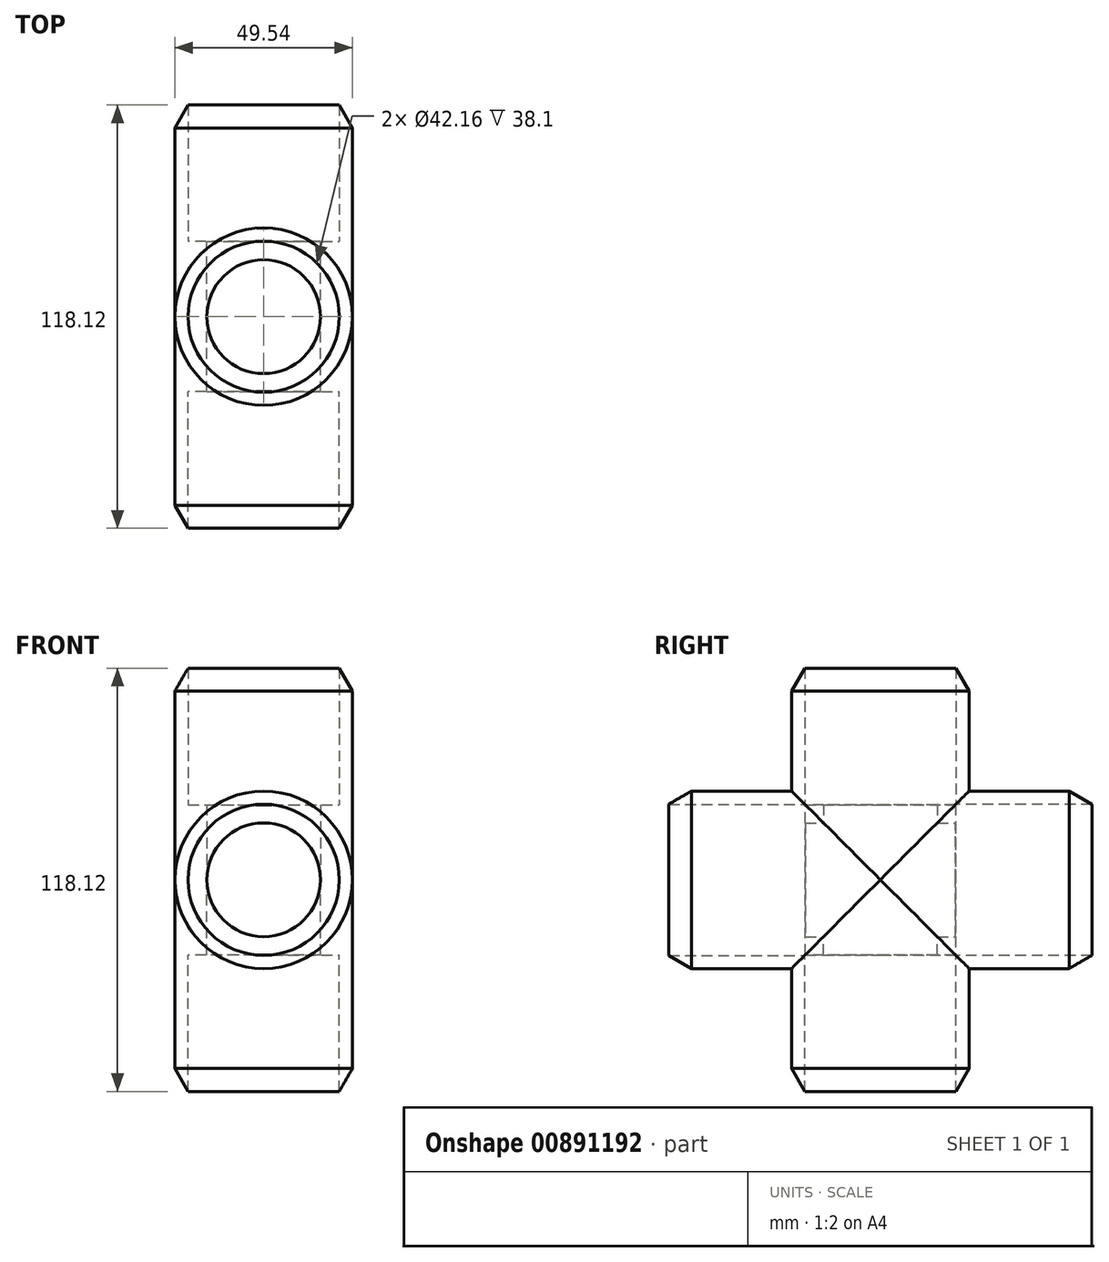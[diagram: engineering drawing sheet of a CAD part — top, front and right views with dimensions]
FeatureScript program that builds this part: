
annotation { "Feature Type Name" : "Feature", "Feature Type Description" : "" }
export const myFeature = defineFeature(function(context is Context, id is Id, definition is map)
    precondition{}
    {
        {
            var Q0;
            Q0=qCreatedBy(makeId("Right.planeOp"),FACE);
            var sketch = newSketch(context, id + "F0", { "sketchPlane" : qUnion([Q0])});
            skLineSegment(sketch, "E0", {"start": v(-59.06, 21.08) * mm, "end": v(-20.96, 21.08) * mm});
            skLineSegment(sketch, "E1", {"start": v(-20.96, 21.08) * mm, "end": v(-20.96, 15.88) * mm});
            skLineSegment(sketch, "E2", {"start": v(-20.96, 15.88) * mm, "end": v(0, 15.88) * mm});
            skLineSegment(sketch, "E3", {"start": v(15.87, 0) * mm, "end": v(15.87, 0) * mm});
            skLineSegment(sketch, "E4", {"start": v(15.87, 0) * mm, "end": v(24.77, 0) * mm});
            skLineSegment(sketch, "E5", {"start": v(24.77, 0) * mm, "end": v(24.77, 0) * mm});
            skLineSegment(sketch, "E6", {"start": v(0, 24.77) * mm, "end": v(-52.68, 24.76) * mm});
            skLineSegment(sketch, "E7", {"start": v(-52.68, 24.76) * mm, "end": v(-59.06, 21.08) * mm});
            skArc(sketch, "E8.filletArc", {"start": v(24.77, 0) * mm, "mid": v(17.51, 17.51) * mm, "end": v(0, 24.77) * mm});
            skArc(sketch, "E9.filletArc", {"start": v(15.88, 0) * mm, "mid": v(11.23, 11.23) * mm, "end": v(0, 15.88) * mm});
            skLineSegment(sketch, "E10", {"start": v(0, 0) * mm, "end": v(0, -11.7) * mm});
            skLineSegment(sketch, "E11", {"start": v(0, 0) * mm, "end": v(10.52, 0) * mm});
            skLineSegment(sketch, "E12", {"start": v(-59.06, 21.08) * mm, "end": v(-59.06, 0) * mm});
            skLineSegment(sketch, "E13", {"start": v(-59.06, 0) * mm, "end": v(15.87, 0) * mm});
            skSolve(sketch);
        }
        {
            var Q0;
            Q0=qCreatedBy(makeId("Right.planeOp"),FACE);
            var sketch = newSketch(context, id + "F1", { "sketchPlane" : qUnion([Q0])});
            skLineSegment(sketch, "E14", {"start": v(-21.08, -59.06) * mm, "end": v(-21.08, -20.96) * mm});
            skLineSegment(sketch, "E15", {"start": v(-21.08, -20.96) * mm, "end": v(-15.88, -20.96) * mm});
            skLineSegment(sketch, "E16", {"start": v(-15.88, -20.96) * mm, "end": v(-15.88, 0) * mm});
            skLineSegment(sketch, "E17", {"start": v(0, 15.88) * mm, "end": v(0, 15.88) * mm});
            skLineSegment(sketch, "E18", {"start": v(0, 15.88) * mm, "end": v(0, 24.77) * mm});
            skLineSegment(sketch, "E19", {"start": v(0, 24.77) * mm, "end": v(0, 24.77) * mm});
            skLineSegment(sketch, "E20", {"start": v(-24.77, 0) * mm, "end": v(-24.76, -52.68) * mm});
            skLineSegment(sketch, "E21", {"start": v(-24.76, -52.68) * mm, "end": v(-21.08, -59.06) * mm});
            skArc(sketch, "E22.filletArc", {"start": v(0, 24.77) * mm, "mid": v(-17.51, 17.51) * mm, "end": v(-24.77, 0) * mm});
            skArc(sketch, "E23.filletArc", {"start": v(0, 15.88) * mm, "mid": v(-11.23, 11.23) * mm, "end": v(-15.88, 0) * mm});
            skLineSegment(sketch, "E24", {"start": v(0, 36.04) * mm, "end": v(0, 0) * mm});
            skLineSegment(sketch, "E25", {"start": v(-2.18, 0) * mm, "end": v(0, 0) * mm});
            skLineSegment(sketch, "E26", {"start": v(-21.08, -59.06) * mm, "end": v(0, -59.06) * mm});
            skLineSegment(sketch, "E27", {"start": v(0, -59.06) * mm, "end": v(0, 15.88) * mm});
            skSolve(sketch);
        }
        {
            var Q0;
            Q0=qCreatedBy(makeId("Right.planeOp"),FACE);
            var sketch = newSketch(context, id + "F2", { "sketchPlane" : qUnion([Q0])});
            skLineSegment(sketch, "E28", {"start": v(59.06, -21.08) * mm, "end": v(20.96, -21.08) * mm});
            skLineSegment(sketch, "E29", {"start": v(20.96, -21.08) * mm, "end": v(20.96, -15.88) * mm});
            skLineSegment(sketch, "E30", {"start": v(20.96, -15.88) * mm, "end": v(0, -15.88) * mm});
            skLineSegment(sketch, "E31", {"start": v(-15.87, 0) * mm, "end": v(-15.87, 0) * mm});
            skLineSegment(sketch, "E32", {"start": v(-15.87, 0) * mm, "end": v(-24.77, 0) * mm});
            skLineSegment(sketch, "E33", {"start": v(-24.77, 0) * mm, "end": v(-24.77, 0) * mm});
            skLineSegment(sketch, "E34", {"start": v(0, -24.77) * mm, "end": v(52.68, -24.76) * mm});
            skLineSegment(sketch, "E35", {"start": v(52.68, -24.77) * mm, "end": v(59.06, -21.08) * mm});
            skArc(sketch, "E36.filletArc", {"start": v(-24.77, 0) * mm, "mid": v(-17.51, -17.51) * mm, "end": v(0, -24.77) * mm});
            skArc(sketch, "E37.filletArc", {"start": v(-15.88, 0) * mm, "mid": v(-11.23, -11.23) * mm, "end": v(0, -15.88) * mm});
            skLineSegment(sketch, "E38", {"start": v(0, 2.6) * mm, "end": v(0, 0) * mm});
            skLineSegment(sketch, "E39", {"start": v(0, 0) * mm, "end": v(10.52, 0) * mm});
            skLineSegment(sketch, "E40", {"start": v(59.06, -21.08) * mm, "end": v(59.06, 0) * mm});
            skLineSegment(sketch, "E41", {"start": v(59.06, 0) * mm, "end": v(-15.87, 0) * mm});
            skSolve(sketch);
        }
        {
            var Q0;
            Q0=qCreatedBy(makeId("Right.planeOp"),FACE);
            var sketch = newSketch(context, id + "F3", { "sketchPlane" : qUnion([Q0])});
            skLineSegment(sketch, "E42", {"start": v(21.08, 59.06) * mm, "end": v(21.08, 20.95) * mm});
            skLineSegment(sketch, "E43", {"start": v(21.08, 20.95) * mm, "end": v(15.88, 20.95) * mm});
            skLineSegment(sketch, "E44", {"start": v(15.88, 20.96) * mm, "end": v(15.88, 0) * mm});
            skLineSegment(sketch, "E45", {"start": v(0, -15.88) * mm, "end": v(0, -15.88) * mm});
            skLineSegment(sketch, "E46", {"start": v(0, -15.88) * mm, "end": v(0, -24.77) * mm});
            skLineSegment(sketch, "E47", {"start": v(0, -24.77) * mm, "end": v(0, -24.77) * mm});
            skLineSegment(sketch, "E48", {"start": v(24.77, 0) * mm, "end": v(24.76, 52.68) * mm});
            skLineSegment(sketch, "E49", {"start": v(24.76, 52.68) * mm, "end": v(21.08, 59.06) * mm});
            skArc(sketch, "E50.filletArc", {"start": v(0, -24.77) * mm, "mid": v(17.51, -17.51) * mm, "end": v(24.77, 0) * mm});
            skArc(sketch, "E51.filletArc", {"start": v(0, -15.88) * mm, "mid": v(11.23, -11.23) * mm, "end": v(15.88, 0) * mm});
            skLineSegment(sketch, "E52", {"start": v(0, 9.3) * mm, "end": v(0, 0) * mm});
            skLineSegment(sketch, "E53", {"start": v(-7.4, 0) * mm, "end": v(0, 0) * mm});
            skLineSegment(sketch, "E54", {"start": v(21.08, 59.05) * mm, "end": v(0, 59.05) * mm});
            skLineSegment(sketch, "E55", {"start": v(0, 59.05) * mm, "end": v(0, -15.88) * mm});
            skSolve(sketch);
        }
        {
            var Q0;
            Q0=qSketchRegion(id+"F0",true);
            var Q1;
            Q1=sQuery(id+"F0.wireOp",EDGE,"E13");
            revolve(context, id + "F4", {"surfaceOperationType" : NewSurfaceOperationType.NEW, "entities" : qUnion([Q0]), "axis" : qUnion([Q1]), "revolveType" : RevolveType.FULL});
        }
        {
            var Q0;
            {var subQ4=makeQuery(id+"F1.imprint","IMPRINT",EDGE,{"derivedFrom":sQuery(id+"F1.wireOp",EDGE,"E14")});Q0=qUnion([makeQuery(id+"F1.imprint","IMPRINT",FACE,{"disambiguationData":[TD([[subQ4,1.0]])]}),makeQuery(id+"F1.imprint","IMPRINT",FACE,{"disambiguationData":[TD([[subQ4,-1.0]])]})]);}
            var Q1;
            Q1=sQuery(id+"F1.wireOp",EDGE,"E27");
            revolve(context, id + "F5", {"operationType" : NewBodyOperationType.ADD, "surfaceOperationType" : NewSurfaceOperationType.NEW, "entities" : qUnion([Q0]), "axis" : qUnion([Q1]), "revolveType" : RevolveType.FULL});
        }
        {
            var Q0;
            Q0=qSketchRegion(id+"F2",true);
            var Q1;
            Q1=sQuery(id+"F2.wireOp",EDGE,"E41");
            revolve(context, id + "F6", {"operationType" : NewBodyOperationType.ADD, "surfaceOperationType" : NewSurfaceOperationType.NEW, "entities" : qUnion([Q0]), "axis" : qUnion([Q1]), "revolveType" : RevolveType.FULL});
        }
        {
            var Q0;
            Q0=qSketchRegion(id+"F3",true);
            var Q1;
            Q1=sQuery(id+"F3.wireOp",EDGE,"E55");
            revolve(context, id + "F7", {"operationType" : NewBodyOperationType.ADD, "surfaceOperationType" : NewSurfaceOperationType.NEW, "entities" : qUnion([Q0]), "axis" : qUnion([Q1]), "revolveType" : RevolveType.FULL});
        }
        {
            var Q0;
            Q0=makeQuery(id+"F0.imprint","IMPRINT",FACE,{"disambiguationData":[TD([[makeQuery(id+"F0.imprint","IMPRINT",EDGE,{"derivedFrom":sQuery(id+"F0.wireOp",EDGE,"E0")}),-1.0]])]});
            var Q1;
            Q1=sQuery(id+"F0.wireOp",EDGE,"E13");
            revolve(context, id + "F8", {"operationType" : NewBodyOperationType.REMOVE, "surfaceOperationType" : NewSurfaceOperationType.NEW, "entities" : qUnion([Q0]), "axis" : qUnion([Q1]), "revolveType" : RevolveType.FULL, "oppositeDirection" : true});
        }
        {
            var Q0;
            Q0=makeQuery(id+"F1.imprint","IMPRINT",FACE,{"disambiguationData":[TD([[makeQuery(id+"F1.imprint","IMPRINT",EDGE,{"derivedFrom":sQuery(id+"F1.wireOp",EDGE,"E14")}),-1.0]])]});
            var Q1;
            Q1=sQuery(id+"F1.wireOp",EDGE,"E27");
            revolve(context, id + "F9", {"operationType" : NewBodyOperationType.REMOVE, "surfaceOperationType" : NewSurfaceOperationType.NEW, "entities" : qUnion([Q0]), "axis" : qUnion([Q1]), "revolveType" : RevolveType.FULL, "oppositeDirection" : true});
        }
        {
            var Q0;
            Q0=makeQuery(id+"F2.imprint","IMPRINT",FACE,{"disambiguationData":[TD([[makeQuery(id+"F2.imprint","IMPRINT",EDGE,{"derivedFrom":sQuery(id+"F2.wireOp",EDGE,"E28")}),-1.0]])]});
            var Q1;
            Q1=sQuery(id+"F2.wireOp",EDGE,"E41");
            revolve(context, id + "F10", {"operationType" : NewBodyOperationType.REMOVE, "surfaceOperationType" : NewSurfaceOperationType.NEW, "entities" : qUnion([Q0]), "axis" : qUnion([Q1]), "revolveType" : RevolveType.FULL, "oppositeDirection" : true});
        }
        {
            var Q0;
            Q0=makeQuery(id+"F3.imprint","IMPRINT",FACE,{"disambiguationData":[TD([[makeQuery(id+"F3.imprint","IMPRINT",EDGE,{"derivedFrom":sQuery(id+"F3.wireOp",EDGE,"E42")}),-1.0]])]});
            var Q1;
            Q1=sQuery(id+"F3.wireOp",EDGE,"E55");
            revolve(context, id + "F11", {"operationType" : NewBodyOperationType.REMOVE, "surfaceOperationType" : NewSurfaceOperationType.NEW, "entities" : qUnion([Q0]), "axis" : qUnion([Q1]), "revolveType" : RevolveType.FULL, "oppositeDirection" : true});
        }
    });
